# Revit family: Plumbing_Valves_Bermad_430_Pressure_Sustaining_Valve Flanged 1.5in-12in
name_source: partatom
category: Pipe Accessories
units: mm (PartAtom-declared; Revit-internal decimal feet)

## family parameters
Always vertical = No
Cut with Voids When Loaded = No
Part Type = Valve - Breaks Into
Round Connector Dimension = Use Diameter
Shared = No
Work Plane-Based = No

## types (9) — shared parameters
Assembly Code = D2020300
Body_Type = Flanged
D_Table = 400 Revit Sizes
Description = Pressure Relief / Sustaining Valve
Flanged_Body = Yes
Grooved_Body = No
M = 160 mm
Manufacturer = Bermad
Max Working Water Pressure = 16.0 bar
Max Working Water Temperature = 50 °C
Model = 430
Product url = www.bermad.com/product/bc-430-p/
T_from_port = 220 mm
Threaded_Body = No
URL = www.Bermad.com

## per-type parameters (varying)
- 1.5" - DN40: Body_Dim=62 mm; CChamper_Rad=11 mm; CPort_Dim=40 mm  [stored 0.131234 ft]; Cover_Dim=118 mm; Flange_Dim=127 mm; Flange_Thick=19 mm  [stored 0.062336 ft]; H=153 mm; H1=19 mm  [stored 0.062336 ft]; H2=20 mm  [stored 0.0656168 ft]; H2_Plus_H3=35 mm  [stored 0.114829 ft]; H3=15 mm  [stored 0.0492126 ft]; H4=16 mm  [stored 0.0524934 ft]; H5=6 mm  [stored 0.019685 ft]; H5_Plus_H6=8 mm  [stored 0.0262467 ft]; H6=2 mm  [stored 0.00656168 ft]; H_Plus_M=313 mm; K Coefficient=4.5; L=205 mm; Nominal_Diameter=40 mm  [stored 0.131234 ft]; Port_Dim=30 mm  [stored 0.0984252 ft]; Port_Down_X=62 mm; Port_Down_Y=5 mm  [stored 0.0164042 ft]; Port_Up_X=53 mm; Port_Up_Y=10 mm  [stored 0.0328084 ft]; Port_W=51 mm; Port_h=41 mm  [stored 0.134514 ft]; Port_h_Dim=45 mm  [stored 0.147638 ft]; Port_h_X=45 mm  [stored 0.147638 ft]; W=127 mm; Weight=8.00 kgf; h=64 mm
- 2" - DN50: Body_Dim=62 mm; CChamper_Rad=11 mm; CPort_Dim=40 mm  [stored 0.131234 ft]; Cover_Dim=118 mm; Flange_Dim=152 mm; Flange_Thick=20 mm  [stored 0.0656168 ft]; H=155 mm; H1=31 mm  [stored 0.101706 ft]; H2=14 mm  [stored 0.0459318 ft]; H2_Plus_H3=28 mm  [stored 0.0918635 ft]; H3=14 mm  [stored 0.0459318 ft]; H4=17 mm  [stored 0.0557743 ft]; H5=4 mm  [stored 0.0131234 ft]; H5_Plus_H6=4 mm  [stored 0.0131234 ft]; H6=0 mm  [stored 0 ft]; H_Plus_M=315 mm; K Coefficient=3; L=205 mm; Nominal_Diameter=50 mm  [stored 0.164042 ft]; Port_Dim=30 mm  [stored 0.0984252 ft]; Port_Down_X=63 mm; Port_Down_Y=2 mm  [stored 0.00656168 ft]; Port_Up_X=58 mm; Port_Up_Y=10 mm  [stored 0.0328084 ft]; Port_W=51 mm; Port_h=47 mm  [stored 0.154199 ft]; Port_h_Dim=40 mm  [stored 0.131234 ft]; Port_h_X=35 mm  [stored 0.114829 ft]; W=152 mm; Weight=9.00 kgf; h=76 mm
- 2.5" - DN65: Body_Dim=67 mm; CChamper_Rad=18 mm  [stored 0.0590551 ft]; CPort_Dim=40 mm  [stored 0.131234 ft]; Cover_Dim=132 mm; Flange_Dim=185 mm; Flange_Thick=20 mm  [stored 0.0656168 ft]; H=180 mm; H1=34 mm; H2=12 mm  [stored 0.0393701 ft]; H2_Plus_H3=32 mm  [stored 0.104987 ft]; H3=20 mm  [stored 0.0656168 ft]; H4=17 mm  [stored 0.0557743 ft]; H5=4 mm  [stored 0.0131234 ft]; H5_Plus_H6=4 mm  [stored 0.0131234 ft]; H6=0 mm  [stored 0 ft]; H_Plus_M=340 mm; K Coefficient=4.6; L=205 mm; Nominal_Diameter=65 mm; Port_Dim=30 mm  [stored 0.0984252 ft]; Port_Down_X=62 mm; Port_Down_Y=6 mm  [stored 0.019685 ft]; Port_Up_X=58 mm; Port_Up_Y=10 mm  [stored 0.0328084 ft]; Port_W=56 mm; Port_h=47 mm  [stored 0.154199 ft]; Port_h_Dim=60 mm; Port_h_X=35 mm  [stored 0.114829 ft]; W=185 mm; Weight=10.50 kgf; h=93 mm
- 3" - DN80: Body_Dim=81 mm; CChamper_Rad=11 mm; CPort_Dim=40 mm  [stored 0.131234 ft]; Cover_Dim=170 mm; Flange_Dim=200 mm; Flange_Thick=20 mm  [stored 0.0656168 ft]; H=210 mm; H1=39 mm  [stored 0.127953 ft]; H2=17 mm  [stored 0.0557743 ft]; H2_Plus_H3=35 mm  [stored 0.114829 ft]; H3=18 mm  [stored 0.0590551 ft]; H4=22 mm  [stored 0.0721785 ft]; H5=9 mm  [stored 0.0295276 ft]; H5_Plus_H6=14 mm  [stored 0.0459318 ft]; H6=5 mm  [stored 0.0164042 ft]; H_Plus_M=370 mm; K Coefficient=3.5; L=257 mm; Nominal_Diameter=80 mm; Port_Dim=30 mm  [stored 0.0984252 ft]; Port_Down_X=71 mm; Port_Down_Y=23 mm; Port_Up_X=70 mm; Port_Up_Y=14 mm  [stored 0.0459318 ft]; Port_W=70 mm; Port_h=59 mm; Port_h_Dim=60 mm; Port_h_X=56 mm; W=200 mm; Weight=19.00 kgf; h=100 mm
- 4" - DN100: Body_Dim=95 mm; CChamper_Rad=14 mm  [stored 0.0459318 ft]; CPort_Dim=40 mm  [stored 0.131234 ft]; Cover_Dim=205 mm; Flange_Dim=232 mm; Flange_Thick=25 mm  [stored 0.082021 ft]; H=252 mm; H1=49 mm  [stored 0.160761 ft]; H2=27 mm  [stored 0.0885827 ft]; H2_Plus_H3=49 mm  [stored 0.160761 ft]; H3=22 mm  [stored 0.0721785 ft]; H4=27 mm  [stored 0.0885827 ft]; H5=6 mm  [stored 0.019685 ft]; H5_Plus_H6=12 mm  [stored 0.0393701 ft]; H6=6 mm  [stored 0.019685 ft]; H_Plus_M=412 mm; K Coefficient=3.8; L=320 mm; Nominal_Diameter=100 mm; Port_Dim=35 mm  [stored 0.114829 ft]; Port_Down_X=95 mm; Port_Down_Y=25 mm  [stored 0.082021 ft]; Port_Up_X=85 mm; Port_Up_Y=17 mm  [stored 0.0557743 ft]; Port_W=90 mm; Port_h=74 mm; Port_h_Dim=80 mm; Port_h_X=70 mm; W=232 mm; Weight=28.00 kgf; h=116 mm
- 6" - DN150: Body_Dim=130 mm; CChamper_Rad=16 mm  [stored 0.0524934 ft]; CPort_Dim=80 mm; Cover_Dim=290 mm; Flange_Dim=286 mm; Flange_Thick=25 mm  [stored 0.082021 ft]; H=345 mm; H1=71 mm; H2=33 mm  [stored 0.108268 ft]; H2_Plus_H3=73 mm; H3=40 mm  [stored 0.131234 ft]; H4=46 mm; H5=11 mm; H5_Plus_H6=11 mm; H6=0 mm  [stored 0 ft]; H_Plus_M=505 mm; K Coefficient=3.8; L=415 mm; Nominal_Diameter=150 mm; Port_Dim=40 mm  [stored 0.131234 ft]; Port_Down_X=120 mm; Port_Down_Y=48 mm  [stored 0.15748 ft]; Port_Up_X=130 mm; Port_Up_Y=25 mm  [stored 0.082021 ft]; Port_W=110 mm; Port_h=95 mm; Port_h_Dim=80 mm; Port_h_X=116 mm; W=290 mm; Weight=68.00 kgf; h=143 mm
- 8" - DN200: Body_Dim=190 mm; CChamper_Rad=56 mm; CPort_Dim=80 mm; Cover_Dim=361 mm; Flange_Dim=344 mm; Flange_Thick=29 mm  [stored 0.0951444 ft]; H=430 mm; H1=101 mm; H2=30 mm  [stored 0.0984252 ft]; H2_Plus_H3=79 mm; H3=49 mm  [stored 0.160761 ft]; H4=61 mm; H5=20 mm  [stored 0.0656168 ft]; H5_Plus_H6=20 mm  [stored 0.0656168 ft]; H6=0 mm  [stored 0 ft]; H_Plus_M=590 mm; K Coefficient=4.1; L=500 mm; Nominal_Diameter=200 mm; Port_Dim=40 mm  [stored 0.131234 ft]; Port_Down_X=150 mm; Port_Down_Y=55 mm; Port_Up_X=150 mm; Port_Up_Y=33 mm  [stored 0.108268 ft]; Port_W=135 mm; Port_h=100 mm; Port_h_Dim=80 mm; Port_h_X=150 mm; W=361 mm; Weight=125.00 kgf; h=172 mm
- 10" - DN250: Body_Dim=200 mm; CChamper_Rad=56 mm; CPort_Dim=80 mm; Cover_Dim=361 mm; Flange_Dim=408 mm; Flange_Thick=31 mm  [stored 0.101706 ft]; H=460 mm; H1=93 mm; H2=39 mm  [stored 0.127953 ft]; H2_Plus_H3=91 mm; H3=52 mm; H4=52 mm; H5=23 mm; H5_Plus_H6=23 mm; H6=0 mm  [stored 0 ft]; H_Plus_M=620 mm; K Coefficient=8.9; L=605 mm; Nominal_Diameter=250 mm; Port_Dim=40 mm  [stored 0.131234 ft]; Port_Down_X=163 mm; Port_Down_Y=62 mm; Port_Up_X=175 mm; Port_Up_Y=42 mm  [stored 0.137795 ft]; Port_W=145 mm; Port_h=142 mm; Port_h_Dim=80 mm; Port_h_X=152 mm; W=408 mm; Weight=140.00 kgf; h=204 mm
- 12" - DN300: Body_Dim=202 mm; CChamper_Rad=56 mm; CPort_Dim=80 mm; Cover_Dim=570 mm; Flange_Dim=485 mm; Flange_Thick=34 mm; H=618 mm; H1=155 mm; H2=53 mm; H2_Plus_H3=91 mm; H3=38 mm  [stored 0.124672 ft]; H4=93 mm; H5=27 mm  [stored 0.0885827 ft]; H5_Plus_H6=28 mm  [stored 0.0918635 ft]; H6=0 mm  [stored 0 ft]; H_Plus_M=778 mm; K Coefficient=3.4; L=731 mm; Nominal_Diameter=300 mm; Port_Dim=60 mm; Port_Down_X=233 mm; Port_Down_Y=70 mm; Port_Up_X=181 mm; Port_Up_Y=70 mm; Port_W=200 mm; Port_h=180 mm; Port_h_Dim=80 mm; Port_h_X=214 mm; W=570 mm; Weight=290.00 kgf; h=243 mm

note: [stored X ft] marks values corroborated as IEEE doubles in the binary element streams (Revit-internal decimal feet)

## geometry (parser evidence)
native form markers: Sweep x1
no freeform markers — native parametric forms only
